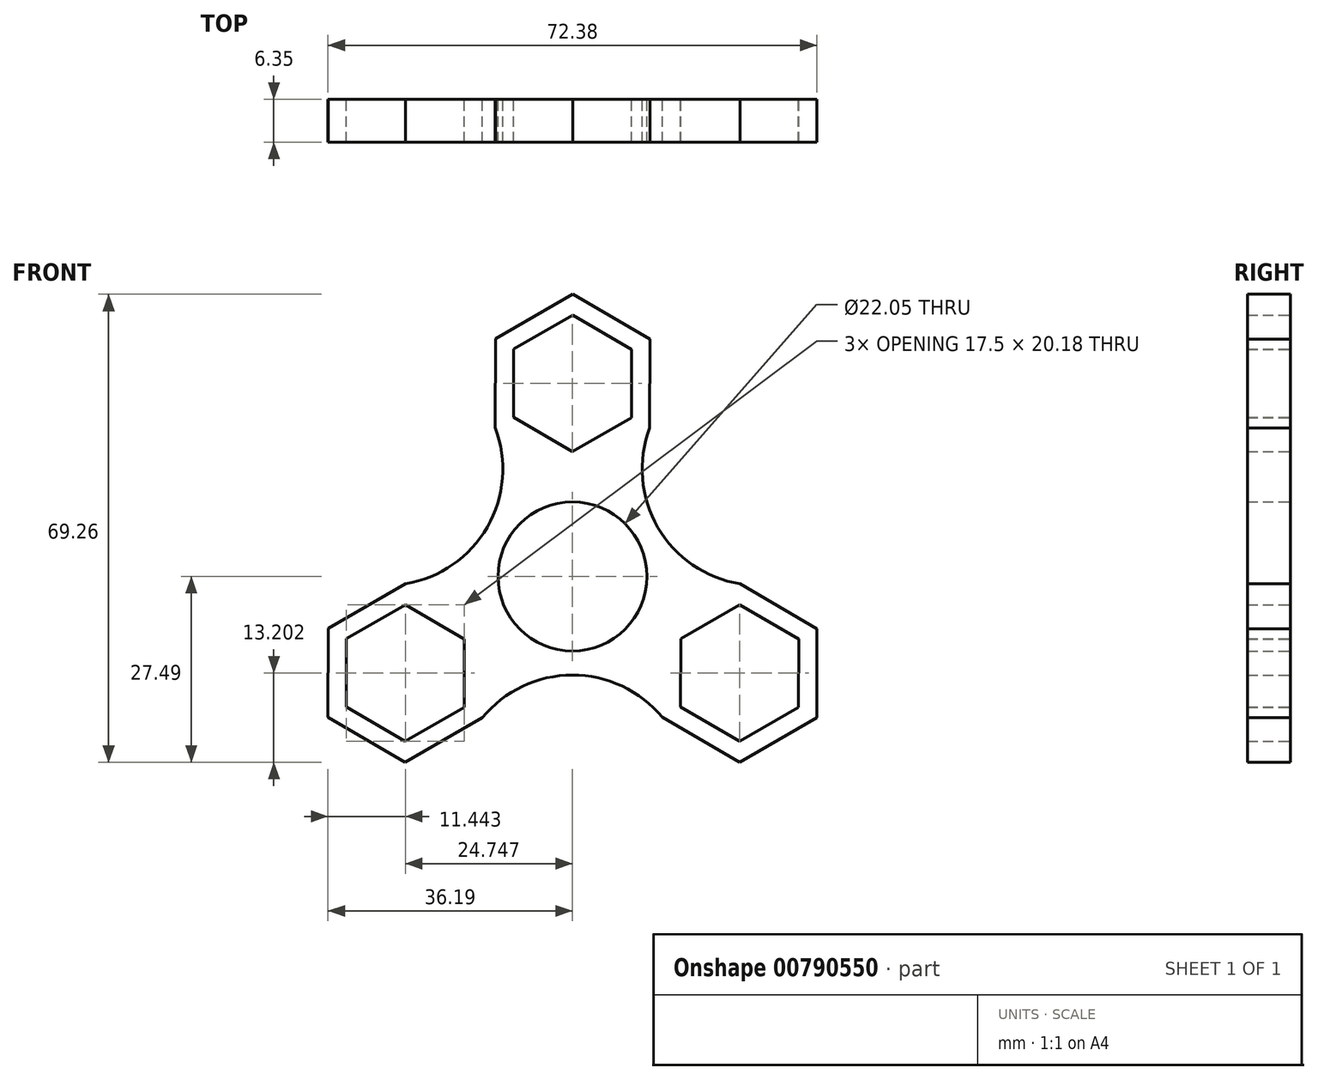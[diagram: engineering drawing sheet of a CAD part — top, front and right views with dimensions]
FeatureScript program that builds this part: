
annotation { "Feature Type Name" : "Feature", "Feature Type Description" : "" }
export const myFeature = defineFeature(function(context is Context, id is Id, definition is map)
    precondition{}
    {
        {
            var Q0;
            Q0=qCreatedBy(makeId("Front.planeOp"),FACE);
            var sketch = newSketch(context, id + "F0", { "sketchPlane" : qUnion([Q0])});
            skCircle(sketch, "E0", {"center": v(0, 0) * mm, "radius": 11.02 * mm});
            skCircle(sketch, "E1", {"center": v(0, 0) * mm, "radius": 14.29 * mm});
            skCircle(sketch, "E2.cCircle", {"center": v(0, 28.58) * mm, "radius": 8.74 * mm, "construction": true});
            skLineSegment(sketch, "E2.0", {"start": v(8.73, 23.5) * mm, "end": v(-0.02, 18.49) * mm});
            skLineSegment(sketch, "E2.1", {"start": v(-0.02, 18.49) * mm, "end": v(-8.75, 23.55) * mm});
            skLineSegment(sketch, "E2.2", {"start": v(-8.75, 23.55) * mm, "end": v(-8.73, 33.64) * mm});
            skLineSegment(sketch, "E2.3", {"start": v(-8.73, 33.64) * mm, "end": v(0.02, 38.66) * mm});
            skLineSegment(sketch, "E2.4", {"start": v(0.02, 38.66) * mm, "end": v(8.75, 33.6) * mm});
            skLineSegment(sketch, "E2.5", {"start": v(8.75, 33.6) * mm, "end": v(8.73, 23.5) * mm});
            skPoint(sketch, "E2.0.midPoint", {"position": v(4.35, 21) * mm});
            skCircle(sketch, "E3.cCircle", {"center": v(0, 28.58) * mm, "radius": 11.43 * mm, "construction": true});
            skLineSegment(sketch, "E3.0", {"start": v(11.41, 21.95) * mm, "end": v(-0.03, 15.38) * mm});
            skLineSegment(sketch, "E3.1", {"start": v(-0.03, 15.38) * mm, "end": v(-11.45, 22) * mm});
            skLineSegment(sketch, "E3.2", {"start": v(-11.45, 22) * mm, "end": v(-11.41, 35.2) * mm});
            skLineSegment(sketch, "E3.3", {"start": v(-11.41, 35.2) * mm, "end": v(0.03, 41.77) * mm});
            skLineSegment(sketch, "E3.4", {"start": v(0.03, 41.77) * mm, "end": v(11.45, 35.15) * mm});
            skLineSegment(sketch, "E3.5", {"start": v(11.45, 35.15) * mm, "end": v(11.41, 21.95) * mm});
            skPoint(sketch, "E3.0.midPoint", {"position": v(5.7, 18.66) * mm});
            skPoint(sketch, "E4.1.0", {"position": v(-19, -4.4) * mm});
            skLineSegment(sketch, "E4.1.1", {"start": v(-33.5, -19.31) * mm, "end": v(-33.47, -9.22) * mm});
            skLineSegment(sketch, "E4.1.2", {"start": v(-13.3, -7.72) * mm, "end": v(-13.33, -20.91) * mm});
            skLineSegment(sketch, "E4.1.3", {"start": v(-16.02, -19.35) * mm, "end": v(-24.77, -24.38) * mm});
            skLineSegment(sketch, "E4.1.4", {"start": v(-24.71, -1.09) * mm, "end": v(-13.3, -7.72) * mm});
            skCircle(sketch, "E4.1.5", {"center": v(-24.75, -14.29) * mm, "radius": 11.43 * mm, "construction": true});
            skLineSegment(sketch, "E4.1.6", {"start": v(-33.47, -9.22) * mm, "end": v(-24.72, -4.2) * mm});
            skCircle(sketch, "E4.1.7", {"center": v(-24.75, -14.29) * mm, "radius": 8.74 * mm, "construction": true});
            skLineSegment(sketch, "E4.1.8", {"start": v(-13.33, -20.91) * mm, "end": v(-24.78, -27.49) * mm});
            skPoint(sketch, "E4.1.9", {"position": v(-20.36, -6.73) * mm});
            skLineSegment(sketch, "E4.1.11", {"start": v(-36.16, -7.66) * mm, "end": v(-24.71, -1.09) * mm});
            skLineSegment(sketch, "E4.1.12", {"start": v(-36.2, -20.86) * mm, "end": v(-36.16, -7.66) * mm});
            skLineSegment(sketch, "E4.1.13", {"start": v(-24.78, -27.49) * mm, "end": v(-36.2, -20.86) * mm});
            skLineSegment(sketch, "E4.1.14", {"start": v(-16, -9.26) * mm, "end": v(-16.02, -19.35) * mm});
            skLineSegment(sketch, "E4.1.15", {"start": v(-24.77, -24.38) * mm, "end": v(-33.5, -19.31) * mm});
            skLineSegment(sketch, "E4.1.16", {"start": v(-24.72, -4.2) * mm, "end": v(-16, -9.26) * mm});
            skPoint(sketch, "E4.2.0", {"position": v(13.32, -14.26) * mm});
            skLineSegment(sketch, "E4.2.1", {"start": v(33.47, -19.35) * mm, "end": v(24.72, -24.38) * mm});
            skLineSegment(sketch, "E4.2.2", {"start": v(13.33, -7.66) * mm, "end": v(24.78, -1.09) * mm});
            skLineSegment(sketch, "E4.2.3", {"start": v(24.77, -4.2) * mm, "end": v(33.5, -9.26) * mm});
            skLineSegment(sketch, "E4.2.4", {"start": v(13.3, -20.86) * mm, "end": v(13.33, -7.66) * mm});
            skCircle(sketch, "E4.2.5", {"center": v(24.75, -14.29) * mm, "radius": 11.43 * mm, "construction": true});
            skLineSegment(sketch, "E4.2.6", {"start": v(24.72, -24.38) * mm, "end": v(16, -19.31) * mm});
            skCircle(sketch, "E4.2.7", {"center": v(24.75, -14.29) * mm, "radius": 8.74 * mm, "construction": true});
            skLineSegment(sketch, "E4.2.8", {"start": v(24.78, -1.09) * mm, "end": v(36.2, -7.72) * mm});
            skPoint(sketch, "E4.2.9", {"position": v(16, -14.27) * mm});
            skLineSegment(sketch, "E4.2.11", {"start": v(24.71, -27.49) * mm, "end": v(13.3, -20.86) * mm});
            skLineSegment(sketch, "E4.2.12", {"start": v(36.16, -20.91) * mm, "end": v(24.71, -27.49) * mm});
            skLineSegment(sketch, "E4.2.13", {"start": v(36.2, -7.72) * mm, "end": v(36.16, -20.91) * mm});
            skLineSegment(sketch, "E4.2.14", {"start": v(16.02, -9.22) * mm, "end": v(24.77, -4.2) * mm});
            skLineSegment(sketch, "E4.2.15", {"start": v(33.5, -9.26) * mm, "end": v(33.47, -19.35) * mm});
            skLineSegment(sketch, "E4.2.16", {"start": v(16, -19.31) * mm, "end": v(16.02, -9.22) * mm});
            skArc(sketch, "E5", {"start": v(-24.71, -1.09) * mm, "mid": v(-12.62, 7.32) * mm, "end": v(-11.45, 22) * mm});
            skArc(sketch, "E6", {"start": v(11.41, 21.95) * mm, "mid": v(12.65, 7.27) * mm, "end": v(24.78, -1.09) * mm});
            skArc(sketch, "E7", {"start": v(13.3, -20.86) * mm, "mid": v(-0.03, -14.58) * mm, "end": v(-13.33, -20.91) * mm});
            skSolve(sketch);
        }
        {
            var Q0;
            Q0=makeQuery(id+"F0.imprint","IMPRINT",FACE,{"disambiguationData":[TD([[makeQuery(id+"F0.imprint","IMPRINT",EDGE,{"derivedFrom":sQuery(id+"F0.wireOp",EDGE,"E4.1.1")}),1.0]])]});
            var Q1;
            Q1=makeQuery(id+"F0.imprint","IMPRINT",FACE,{"disambiguationData":[TD([[makeQuery(id+"F0.imprint","IMPRINT",EDGE,{"derivedFrom":sQuery(id+"F0.wireOp",EDGE,"E1")}),1.0]])]});
            var Q2;
            Q2=makeQuery(id+"F0.imprint","IMPRINT",FACE,{"disambiguationData":[TD([[makeQuery(id+"F0.imprint","IMPRINT",EDGE,{"derivedFrom":sQuery(id+"F0.wireOp",EDGE,"E1")}),-1.0]])]});
            var Q3;
            Q3=makeQuery(id+"F0.imprint","IMPRINT",FACE,{"disambiguationData":[TD([[makeQuery(id+"F0.imprint","IMPRINT",EDGE,{"derivedFrom":sQuery(id+"F0.wireOp",EDGE,"E4.2.1")}),1.0]])]});
            var Q4;
            Q4=makeQuery(id+"F0.imprint","IMPRINT",FACE,{"disambiguationData":[TD([[makeQuery(id+"F0.imprint","IMPRINT",EDGE,{"derivedFrom":sQuery(id+"F0.wireOp",EDGE,"E2.0")}),1.0]])]});
            extrude(context, id + "F1", {"entities" : qUnion([Q0, Q1, Q2, Q3, Q4]), "depth" : 6.35 * mm, "offsetDistance" : 25.4 * mm});
        }
    });
